# Revit family: PlumFix_Sink_ABEY_Entry_Project 175 Sink_Left Bowl_Face Based
name_source: partatom
category: Plumbing Fixtures
revit_build: Autodesk Revit 2016 (Build: 20170117_1200(x64)
units: mm (PartAtom-declared; Revit-internal decimal feet)

## family parameters
Cut with Voids When Loaded = Yes
Host = Face
OmniClass Number = 23.45.05.14.14
OmniClass Title = Sinks/Lavatories
Part Type = Normal
Room Calculation Point = No
Round Connector Dimension = Use Diameter
Shared = No

## types (1)
- Left Bowl
    CW Connection = No
    CWFU = 0
    Cost = 0 $
    Default Elevation = 900 mm
    Description = Entry 1 & 3/4 Bowl Kitchen Sink - Left Bowl
    HW Connection = No
    HWFU = 0
    Manufacturer = Abey Australia
    Manufacturer_Overall Depth = 480 mm  [stored 1.5748 ft]
    Manufacturer_Overall Height = 177 mm  [stored 0.580709 ft]
    Manufacturer_Overall Width = 1080 mm  [stored 3.54331 ft]
    Manufacturer_Spec Code = EN175L
    Manufacturer_URL__Product Specific = https://www.abey.com.au
    Model = EN175L
    PlumbingMaterial_ANZRS = z_Abey_Stainless Steel
    Type Comments = Left Bowl
    URL = https://www.abey.com.au
    Vent Connection = No
    WFU = 0
    Waste Connection = Yes

note: [stored X ft] marks values corroborated as IEEE doubles in the binary element streams (Revit-internal decimal feet)

## geometry (parser evidence)
native form markers: Sweep x4
no freeform markers — native parametric forms only
